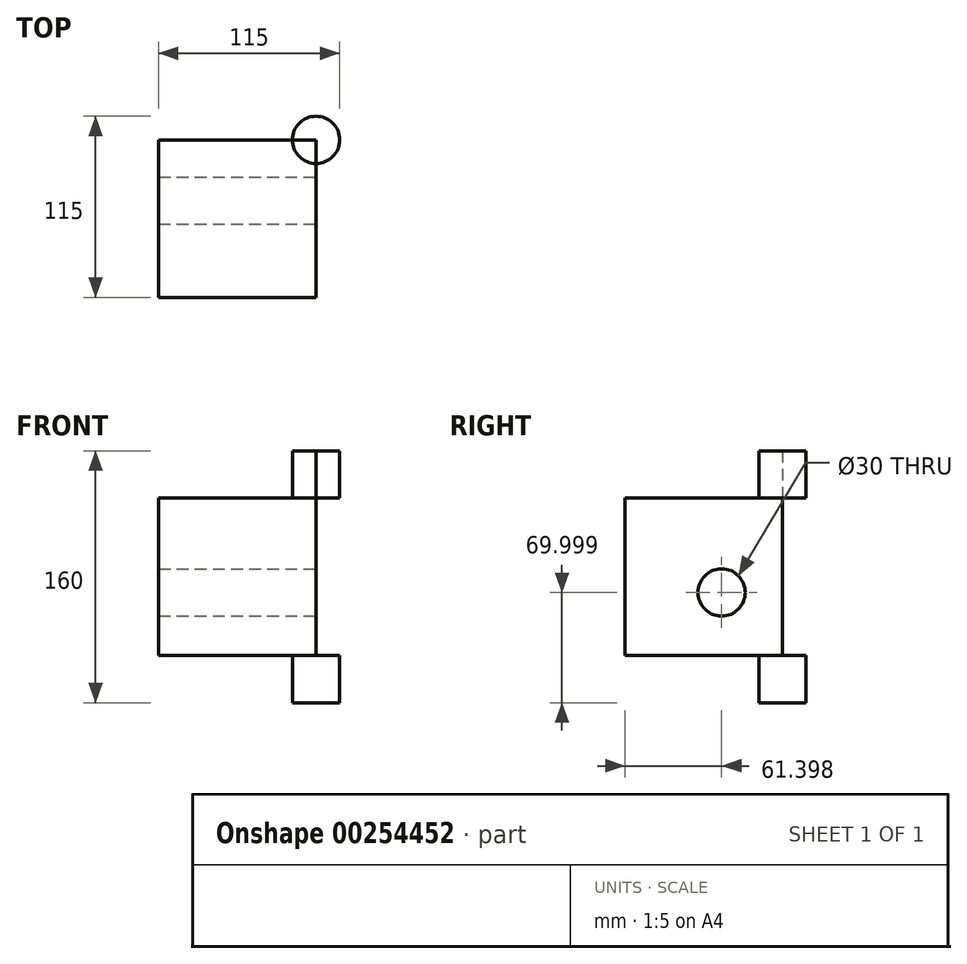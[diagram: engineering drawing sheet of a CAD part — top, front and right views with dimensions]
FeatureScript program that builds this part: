
annotation { "Feature Type Name" : "Feature", "Feature Type Description" : "" }
export const myFeature = defineFeature(function(context is Context, id is Id, definition is map)
    precondition{}
    {
        {
            var Q0;
            Q0=qCreatedBy(makeId("Front.planeOp"),FACE);
            var sketch = newSketch(context, id + "F0", { "sketchPlane" : qUnion([Q0])});
            skLineSegment(sketch, "E0.bottom", {"start": v(0, 0) * mm, "end": v(-100, 0) * mm});
            skLineSegment(sketch, "E0.top", {"start": v(0, 100) * mm, "end": v(-100, 100) * mm});
            skLineSegment(sketch, "E0.left", {"start": v(0, 0) * mm, "end": v(0, 100) * mm});
            skLineSegment(sketch, "E0.right", {"start": v(-100, 0) * mm, "end": v(-100, 100) * mm});
            skSolve(sketch);
        }
        {
            var Q0;
            Q0=makeQuery(id+"F0.imprint","IMPRINT",FACE,{"disambiguationData":[TD([[makeQuery(id+"F0.imprint","IMPRINT",EDGE,{"derivedFrom":sQuery(id+"F0.wireOp",EDGE,"E0.bottom")}),-1.0]])]});
            extrude(context, id + "F1", {"entities" : qUnion([Q0]), "depth" : 100 * mm});
        }
        {
            var Q0;
            Q0=makeQuery(id+"F1.opExtrude","SWEPT_FACE",FACE,{"disambiguationData":[OSD([sQuery(id+"F0.wireOp",EDGE,"E0.top")])]});
            var sketch = newSketch(context, id + "F2", { "sketchPlane" : qUnion([Q0])});
            skCircle(sketch, "E1", {"center": v(0, 0) * mm, "radius": 15 * mm});
            skSolve(sketch);
        }
        {
            var Q0;
            {var subQ0=sQuery(id+"F2.wireOp",EDGE,"E1");var subQ1=sQuery(id+"F0.wireOp",EDGE,"E0.top");var subQ4=makeQuery(id+"F1.opExtrude","CAP_EDGE",EDGE,{"disambiguationData":[OSD([subQ1])],"isStart":true});var subQ5=makeQuery(id+"F2.imprint","INTERSECT",VERTEX,{"derivedFrom":[subQ4,subQ0]});Q0=makeQuery(id+"F2.imprint","IMPRINT",FACE,{"disambiguationData":[TD([[makeQuery(id+"F2.imprint","IMPRINT",EDGE,{"disambiguationData":[TD([[subQ5,1.0]])],"derivedFrom":subQ0}),1.0]])]});}
            extrude(context, id + "F3", {"entities" : qUnion([Q0]), "depth" : 30 * mm});
        }
        {
            var Q0;
            {var subQ0=sQuery(id+"F2.wireOp",EDGE,"E1");var subQ1=sQuery(id+"F0.wireOp",EDGE,"E0.top");var subQ4=makeQuery(id+"F1.opExtrude","CAP_EDGE",EDGE,{"disambiguationData":[OSD([subQ1])],"isStart":true});var subQ5=makeQuery(id+"F2.imprint","INTERSECT",VERTEX,{"derivedFrom":[subQ4,subQ0]});Q0=makeQuery(id+"F2.imprint","IMPRINT",FACE,{"disambiguationData":[TD([[makeQuery(id+"F2.imprint","IMPRINT",EDGE,{"disambiguationData":[TD([[subQ5,-1.0]])],"derivedFrom":subQ0}),1.0]])]});}
            extrude(context, id + "F4", {"entities" : qUnion([Q0]), "depth" : 30 * mm});
        }
        {
            var Q0;
            Q0=makeQuery(id+"F1.opExtrude","SWEPT_FACE",FACE,{"disambiguationData":[OSD([sQuery(id+"F0.wireOp",EDGE,"E0.bottom")])]});
            var sketch = newSketch(context, id + "F5", { "sketchPlane" : qUnion([Q0])});
            skCircle(sketch, "E2", {"center": v(0, 0) * mm, "radius": 15 * mm});
            skSolve(sketch);
        }
        {
            var Q0;
            {var subQ0=sQuery(id+"F5.wireOp",EDGE,"E2");var subQ1=sQuery(id+"F0.wireOp",EDGE,"E0.bottom");var subQ4=makeQuery(id+"F1.opExtrude","CAP_EDGE",EDGE,{"disambiguationData":[OSD([subQ1])],"isStart":true});var subQ5=makeQuery(id+"F5.imprint","INTERSECT",VERTEX,{"derivedFrom":[subQ4,subQ0]});Q0=makeQuery(id+"F5.imprint","IMPRINT",FACE,{"disambiguationData":[TD([[makeQuery(id+"F5.imprint","IMPRINT",EDGE,{"disambiguationData":[TD([[subQ5,-1.0]])],"derivedFrom":subQ0}),1.0]])]});}
            var Q1;
            {var subQ0=sQuery(id+"F5.wireOp",EDGE,"E2");var subQ1=sQuery(id+"F0.wireOp",EDGE,"E0.bottom");var subQ4=makeQuery(id+"F1.opExtrude","CAP_EDGE",EDGE,{"disambiguationData":[OSD([subQ1])],"isStart":true});var subQ5=makeQuery(id+"F5.imprint","INTERSECT",VERTEX,{"derivedFrom":[subQ4,subQ0]});Q1=makeQuery(id+"F5.imprint","IMPRINT",FACE,{"disambiguationData":[TD([[makeQuery(id+"F5.imprint","IMPRINT",EDGE,{"disambiguationData":[TD([[subQ5,1.0]])],"derivedFrom":subQ0}),1.0]])]});}
            extrude(context, id + "F6", {"entities" : qUnion([Q0, Q1]), "operationType" : NewBodyOperationType.ADD, "depth" : 30 * mm});
        }
        {
            var Q0;
            Q0=makeQuery(id+"F1.opExtrude","SWEPT_FACE",FACE,{"disambiguationData":[OSD([sQuery(id+"F0.wireOp",EDGE,"E0.left")])]});
            var sketch = newSketch(context, id + "F7", { "sketchPlane" : qUnion([Q0])});
            skCircle(sketch, "E3", {"center": v(-38.6, 40) * mm, "radius": 15 * mm});
            skSolve(sketch);
        }
        {
            var Q0;
            Q0=sQuery(id+"F7.wireOp",VERTEX,"E3.center");
            var Q1;
            Q1=makeQuery(id+"F1.opExtrude","SWEPT_BODY",BODY,{"disambiguationData":[OSD([sQuery(id+"F0.wireOp",EDGE,"E0.bottom"),sQuery(id+"F0.wireOp",EDGE,"E0.top"),sQuery(id+"F0.wireOp",EDGE,"E0.left"),sQuery(id+"F0.wireOp",EDGE,"E0.right")])]});
            hole(context, id + "F8", {"style" : HoleStyle.SIMPLE, "endStyle" : HoleEndStyle.THROUGH, "holeDiameter" : 30 * mm, "tappedDepth" : 12.7 * mm, "tapClearance" : 3, "locations" : qUnion([Q0]), "scope" : qUnion([Q1])});
        }
    });
